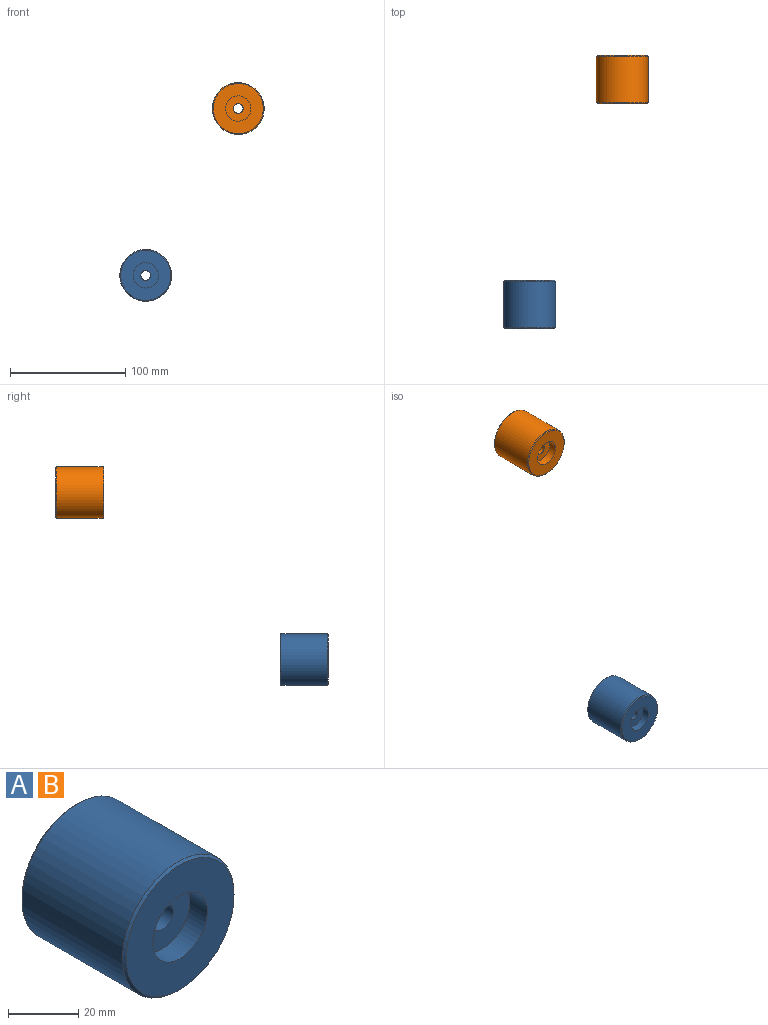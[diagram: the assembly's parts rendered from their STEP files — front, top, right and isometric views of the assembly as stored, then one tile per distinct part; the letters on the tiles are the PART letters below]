
ASSEMBLY  parts=2 mates=2
PART A: 10 faces, bbox 45x42x45 mm
  f0: cylinder r=4.25mm len=28mm, axis (0,1,0), area 747.7mm2, adj f5,f7
  f1: cylinder r=22.5mm len=45mm, axis (0,1,0), area 5725.6mm2, adj f8,f9
  f2: plane 43.5x43.5mm, normal (0,-1,0), area 1106mm2, adj f4,f8
  f3: plane 43.5x43.5mm, normal (0,1,0), area 1106mm2, adj f6,f9
  f4: cylinder r=11mm len=22mm, axis (0,-1,0), area 483.8mm2, adj f2,f5
  f5: plane 22x22mm, normal (0,-1,0), area 323.4mm2, adj f0,f4
  f6: cylinder r=11mm len=22mm, axis (0,1,0), area 483.8mm2, adj f3,f7
  f7: plane 22x22mm, normal (0,1,0), area 323.4mm2, adj f0,f6
  f8: cone r=21.75mm half-angle=45deg, axis (0,1,0), area 147.4mm2, adj f1,f2
  f9: cone r=22.5mm half-angle=45deg, axis (0,-1,0), area 147.4mm2, adj f1,f3
PART B: same geometry as A
PLACE A at identity fixed
PLACE B rot(axis=(0,-1,0),33.2deg) t=(80.39,195,144.95)mm
MATE parallel A.f1 <-> B.f1  axis (0,1,0) through (0,-21,0)mm
MATE parallel B.f1 <-> A.f1  axis (0,1,0) through (80.39,174,144.95)mm
